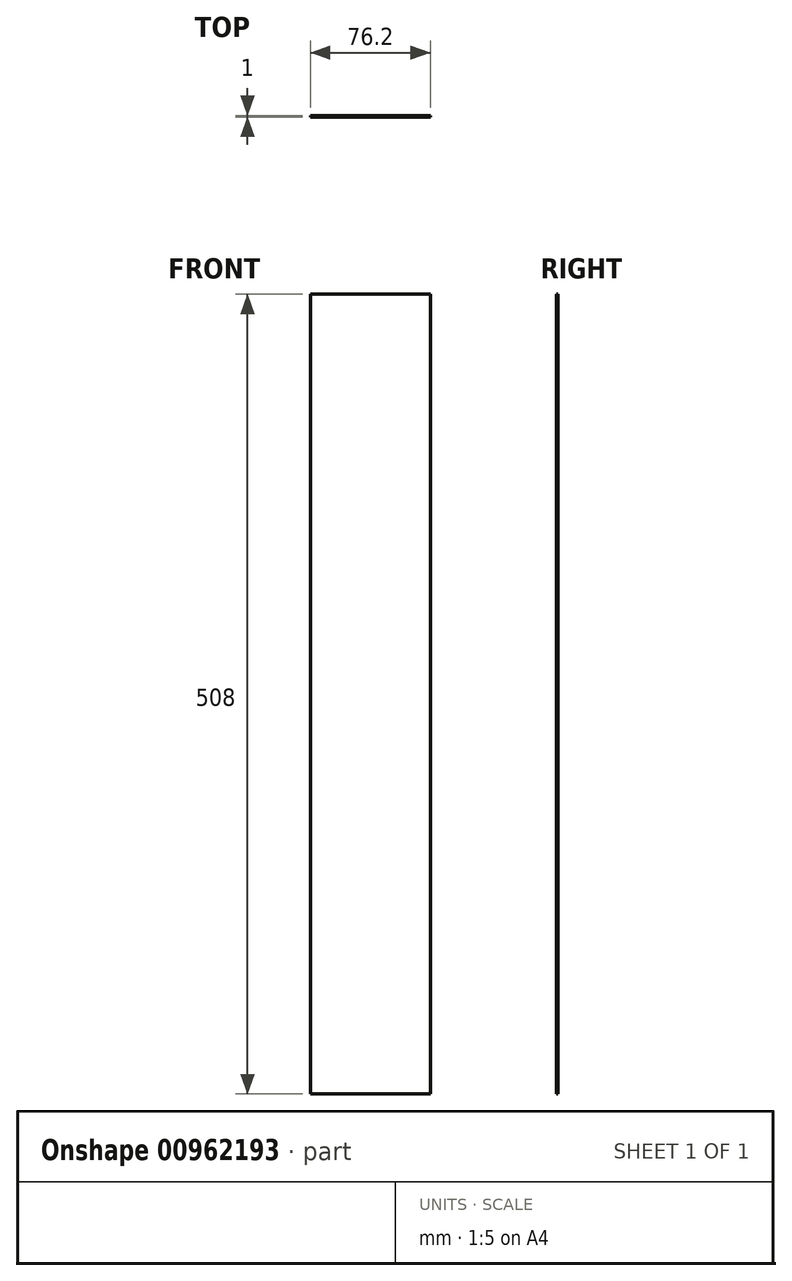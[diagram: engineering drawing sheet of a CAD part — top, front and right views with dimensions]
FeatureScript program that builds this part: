
annotation { "Feature Type Name" : "Feature", "Feature Type Description" : "" }
export const myFeature = defineFeature(function(context is Context, id is Id, definition is map)
    precondition{}
    {
        {
            assignVariable(context, id + "F0", {"name" : "Thickness", "anyValue" : 1});
        }
        {
            var Q0;
            Q0=qCreatedBy(makeId("Front.planeOp"),FACE);
            var sketch = newSketch(context, id + "F1", { "sketchPlane" : qUnion([Q0])});
            skLineSegment(sketch, "E0.bottom", {"start": v(0, 0) * mm, "end": v(76.2, 0) * mm});
            skLineSegment(sketch, "E0.top", {"start": v(0, -508) * mm, "end": v(76.2, -508) * mm});
            skLineSegment(sketch, "E0.left", {"start": v(0, 0) * mm, "end": v(0, -508) * mm});
            skLineSegment(sketch, "E0.right", {"start": v(76.2, 0) * mm, "end": v(76.2, -508) * mm});
            skSolve(sketch);
        }
        {
            var Q0;
            Q0=makeQuery(id+"F1.imprint","IMPRINT",FACE,{"disambiguationData":[TD([[makeQuery(id+"F1.imprint","IMPRINT",EDGE,{"derivedFrom":sQuery(id+"F1.wireOp",EDGE,"E0.bottom")}),-1.0]])]});
            extrude(context, id + "F2", {"entities" : qUnion([Q0]), "depth" : (getVariable(context, 'Thickness')) * mm, "offsetDistance" : 25.4 * mm});
        }
    });
